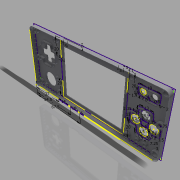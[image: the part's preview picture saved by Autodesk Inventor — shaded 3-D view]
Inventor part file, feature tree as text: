
AUTODESK INVENTOR PART (.ipt)
format: ipt  version: 2019 (Build 230136000, 136)  size: 1,543,168 bytes
history: native  units: mm
features: extrude x31, sketch x28, chamfer x17, fillet x14, hole x2
ambient origin geometry x8: Origin, YZ Plane, XZ Plane, XY Plane, X Axis, Y Axis, Z Axis, Center Point
bodies: Solid1 (feature_tree)
feature tree (92):
  sketch  "Sketch1"  dims[d0=154.0mm d1=68.0mm]
  extrude  "Extrusion1"  Depth=68.0mm
  extrude  "Extrusion2"  Depth=1.0mm
  extrude  "Extrusion3"  Depth=5.2mm TaperAngle=0.0deg
  fillet  "Fillet2"  Radius=1.3mm
  fillet  "Fillet3"  Radius=1.0mm
  fillet  "Fillet9"  Radius=0.75mm
  fillet  "Fillet4"  Radius=29.0mm
  sketch  "Sketch4"  dims[d4=1.0mm d31=5.2mm d32=0.0mm d33=1.3mm d34=0.0mm d40=1.0mm d41=0.0mm d42=0.75mm d43=29.0mm]
  extrude  "Extrusion8"  Depth=29.0mm
  sketch  "Sketch10"  dims[d46=29.0mm d47=29.0mm]
  sketch  "Sketch11"  dims[d48=29.0mm]
  extrude  "Extrusion9"  Depth=29.0mm
  chamfer  "Chamfer1"  Distance=3.9mm
  fillet  "Fillet5"  Radius=4.25mm
  extrude  "Extrusion10"  Depth=2.6mm
  extrude  "Extrusion11"  Depth=0.1mm
  hole  "Hole3"  [1 undecoded]
  fillet  "Fillet10"  Radius=18.0mm
  extrude  "Extrusion12"  Depth=0.1mm
  fillet  "Fillet11"  Radius=2.0mm
  fillet  "Fillet12"  Radius=2.0mm
  extrude  "Extrusion13"  Depth=0.1mm
  extrude  "Extrusion14"  Depth=0.1mm
  fillet  "Fillet13"  Radius=3.25mm
  chamfer  "Chamfer2"  Distance=3.25mm
  sketch  "Sketch16"  dims[d53=5.0mm]
  extrude  "Extrusion15"  Depth=0.1mm
  sketch  "Sketch17"  dims[d62=0.5mm]
  sketch  "Sketch18"  dims[d63=4.0mm]
  extrude  "Extrusion19"  Depth=0.1mm
  extrude  "Extrusion20"  Depth=0.1mm
  chamfer  "Chamfer3"  Distance=9.25mm
  chamfer  "Chamfer4"  Distance=7.0mm
  chamfer  "Chamfer5"  Distance=11.1mm
  chamfer  "Chamfer6"  Distance=15.5mm
  extrude  "Extrusion17"  Depth=0.1mm
  extrude  "Extrusion16"  Depth=0.1mm
  extrude  "Extrusion18"  Depth=0.1mm
  chamfer  "Chamfer8"  Distance=1.1mm
  sketch  "Sketch19"  dims[d64=5.0mm]
  extrude  "Extrusion21"  Depth=6.5mm
  sketch  "Sketch21"  dims[d123=1.0mm]
  extrude  "Extrusion22"  Depth=6.5mm
  sketch  "Sketch22"  dims[d124=6.5mm]
  extrude  "Extrusion23"  Depth=0.1mm TaperAngle=0.0deg
  hole  "Hole2"  [1 undecoded]
  extrude  "Extrusion24"  Depth=6.5mm
  extrude  "Extrusion25"  Depth=0.1mm
  extrude  "Extrusion26"  Depth=6.5mm
  sketch  "Sketch25"  dims[d127=6.5mm]
  extrude  "Extrusion27"  Depth=0.1mm TaperAngle=0.0deg
  extrude  "Extrusion28"  Depth=0.1mm
  fillet  "Fillet15"  Radius=17.25mm
  chamfer  "Chamfer12"  Distance=8.3mm
  extrude  "Extrusion29"  Depth=0.1mm
  fillet  "Fillet16"  Radius=8.6mm
  fillet  "Fillet17"  Radius=8.6mm
  fillet  "Fillet18"  Radius=8.3mm
  extrude  "Extrusion30"  Depth=0.1mm
  extrude  "Extrusion31"  Depth=0.1mm
  extrude  "Extrusion32"  Depth=0.1mm
  fillet  "Fillet19"  Radius=12.0mm
  sketch  "Sketch30"  dims[d132=6.5mm]
  extrude  "Extrusion33"  Depth=0.1mm
  sketch  "Sketch31"  dims[d133=6.5mm d134=3.9mm d135=0.0mm d136=4.25mm]
  extrude  "Extrusion34"  Depth=5.2mm
  chamfer  "Chamfer15"  Distance=5.2mm
  extrude  "Extrusion35"  Depth=0.1mm
  chamfer  "Chamfer16"  Distance=5.0mm
  chamfer  "Chamfer17"  Distance=21.0mm
  chamfer  "Chamfer18"  Distance=5.0mm
  chamfer  "Chamfer19"  Distance=3.0mm
  chamfer  "Chamfer20"  Distance=3.0mm
  chamfer  "Chamfer21"  Distance=7.5mm
  chamfer  "Chamfer22"  Distance=3.0mm
  chamfer  "Chamfer23"  Distance=3.0mm
  sketch  "Sketch2"  dims[d2=1.0mm d3=1.0mm]
  sketch  "Sketch9"  dims[d44=86.0mm d45=29.0mm]
  sketch  "Sketch12"  dims[d49=86.0mm]
  sketch  "Sketch13"  dims[d50=29.0mm]
  sketch  "Sketch14"  dims[d51=29.0mm]
  sketch  "Sketch15"  dims[d52=5.0mm]
  sketch  "Sketch20"  dims[d65=1.75mm]
  sketch  "Sketch23"  dims[d125=6.5mm]
  sketch  "Sketch24"  dims[d126=6.5mm]
  sketch  "Sketch26"  dims[d128=6.5mm]
  sketch  "Sketch27"  dims[d129=6.5mm]
  sketch  "Sketch28"  dims[d130=6.5mm]
  sketch  "Sketch29"  dims[d131=6.5mm]
  sketch  "Sketch32"  dims[d137=4.25mm d138=6.0mm d139=7.28mm d140=2.1mm d141=90.0deg d142=2.6mm d143=0.0mm d144=37.5mm]
  sketch  "Sketch33"  dims[d145=37.5mm d148=18.0mm d149=23.0mm d150=18.0mm d151=12.0mm d152=2.0mm d153=2.0mm d154=2.0mm d155=2.0mm d156=3.25mm d158=3.25mm d160=9.25mm d161=9.25mm d162=9.25mm d163=9.25mm d164=7.0mm d166=11.1mm d168=15.5mm d169=9.25mm d170=1.1mm d171=6.9mm d172=1.1mm d173=6.5mm d175=6.5mm d176=0.7mm d177=0.0mm d178=0.7mm d179=2.0mm d180=45.0deg d181=6.5mm d182=6.0mm d183=6.5mm d184=2.0mm d185=0.0mm d190=24.0mm d191=17.25mm d193=8.3mm d194=8.3mm d195=8.6mm d196=8.6mm d197=8.3mm d198=8.3mm d199=8.1mm d200=8.1mm d201=12.0mm d202=17.0mm d203=5.2mm d204=5.2mm d205=5.0mm d206=5.0mm d207=21.0mm d208=5.0mm d209=3.0mm d210=3.0mm d211=7.5mm d212=3.0mm d213=3.0mm d214=3.9mm d215=0.0mm d216=1.1mm d217=5.0mm d218=4.0mm d219=2.0mm d220=90.0deg d221=2.75mm d222=0.0mm d223=0.5mm d224=14.0mm d225=0.2mm d226=0.0mm d227=2.0mm d228=0.5mm d229=71.0mm d230=53.5mm d234=3.0mm d235=0.0mm d236=77.1mm d237=64.1mm d238=3.05mm d239=2.96mm d240=1.0mm d241=0.0mm d242=0.5mm d243=0.3mm d244=2.0mm d245=45.0deg d249=1.0mm d250=20.0mm d251=20.0mm d252=2.5mm d253=0.0mm d254=1.0mm d255=20.0mm d256=20.0mm d257=0.5mm d258=3.5mm d259=13.962634mm d260=0.5mm d261=3.5mm d262=13.962634mm d263=5.0mm d264=5.0mm d265=0.5mm d266=3.5mm d267=13.962634mm d272=0.25mm d273=3.5mm d274=13.962634mm d275=0.0mm d276=0.0mm d277=3.35mm d278=3.35mm d279=1.4mm d280=0.0mm d281=4.5mm d282=4.5mm d283=3.9mm d284=0.0mm d285=5.0mm d286=0.0mm d290=0.25mm d291=3.0mm d292=13.962634mm d293=0.5mm d294=1.8mm d295=4.75mm d296=0.5mm d297=1.8mm d298=80.0mm d300=4.145mm d301=10.0mm d303=10.0mm d308=0.5mm d309=1.8mm d310=0.5mm d311=1.8mm d312=80.0mm d314=4.14mm d315=10.0mm d317=10.0mm d319=2.6mm d320=0.0mm d321=2.6mm d322=0.0mm d323=0.0mm d324=0.0mm d325=0.0mm d326=1.8mm d327=0.5mm d328=4.75mm d329=130.0mm d331=4.835mm d332=10.0mm d334=10.0mm d336=1.8mm d337=0.5mm d338=4.75mm d339=130.0mm d341=4.835mm d342=10.0mm d344=10.0mm d346=24.0mm d347=6.0mm d348=26.675mm d349=1.375mm d350=0.5mm d351=0.0mm d352=19.0mm d353=9.0mm d354=1.9mm d355=1.9mm d356=2.0mm d357=0.5mm d358=2.6mm d359=0.0mm d360=28.5mm d361=13.0mm d362=13.0mm d363=27.5mm d364=7.75mm d365=7.25mm d366=1.5mm d367=1.5mm d368=1.0mm d369=3.0mm d370=0.5mm d371=2.6mm d372=0.0mm d373=3.0mm d374=5.25mm d375=2.6mm d376=0.0mm d377=6.9mm d378=5.9mm d381=0.5mm d382=1.0mm d383=0.5mm d384=2.1mm d385=0.0mm d403=2.75mm d409=24.0mm d410=2.0mm d411=17.453293mm d412=13.962634mm d413=13.962634mm d415=24.0mm d416=2.75mm d417=2.0mm d418=2.0mm d419=0.5mm d420=2.6mm d421=0.0mm d422=7.599654mm d423=7.6mm d424=7.6mm d425=7.6mm d426=1.0mm d427=2.0mm d428=9.0mm d429=0.5mm d430=6.0mm d431=5.0mm d432=10.0mm d433=14.0mm d434=37.0mm d435=54.5mm d436=67.5mm d437=1.0mm d438=0.0mm d449=10.0mm d450=0.0mm d451=0.5mm d452=0.0mm d453=0.75mm d454=0.5mm d455=1.0mm d456=45.0deg d463=7.0mm d464=1.0mm d465=1.0mm d466=3.0mm d467=3.9mm d468=1.5mm d469=1.45mm d470=1.0mm d471=2.1mm d472=0.0mm d473=10.5mm d474=0.5mm d475=0.5mm d476=1.0mm d477=0.0mm d478=0.0mm d479=20.0mm d480=18.0mm d481=2.1mm d482=0.0mm d483=10.0mm d484=10.0mm d485=5.0mm d486=5.0mm d487=3.0mm d488=0.0mm d489=3.3mm d490=3.8mm d491=1.0mm d492=2.0mm d493=1.0mm d494=0.0mm d495=0.5mm d496=0.75mm d497=0.0mm d498=0.765mm d499=0.5mm d500=1.6mm d501=0.0mm d502=0.5mm d503=2.0mm d504=3.490659mm d505=2.35mm d506=2.35mm d511=0.15mm d512=0.4mm d513=2.5mm d514=0.0mm d516=2.0mm d517=0.1mm d518=45.0deg d519=0.4mm d520=0.15mm d521=0.15mm d522=0.4mm d523=0.4mm d524=0.15mm d525=2.0mm d526=0.1mm d527=45.0deg d528=2.0mm d529=0.1mm d530=45.0deg d531=2.0mm d532=0.1mm d533=45.0deg d534=0.15mm d535=0.4mm d536=0.15mm d537=0.4mm d538=0.4mm d539=0.15mm d540=0.4mm d541=0.15mm d542=2.0mm d543=0.1mm d544=45.0deg d545=2.0mm d546=0.1mm d547=45.0deg d548=2.0mm d549=0.1mm d550=45.0deg d551=2.0mm d552=0.1mm d553=45.0deg]
note: 2 required parameter values undecoded (feature->parameter linkage not recoverable at this tier; creation-order binding heuristic only, values carry confidence <= 0.55)
